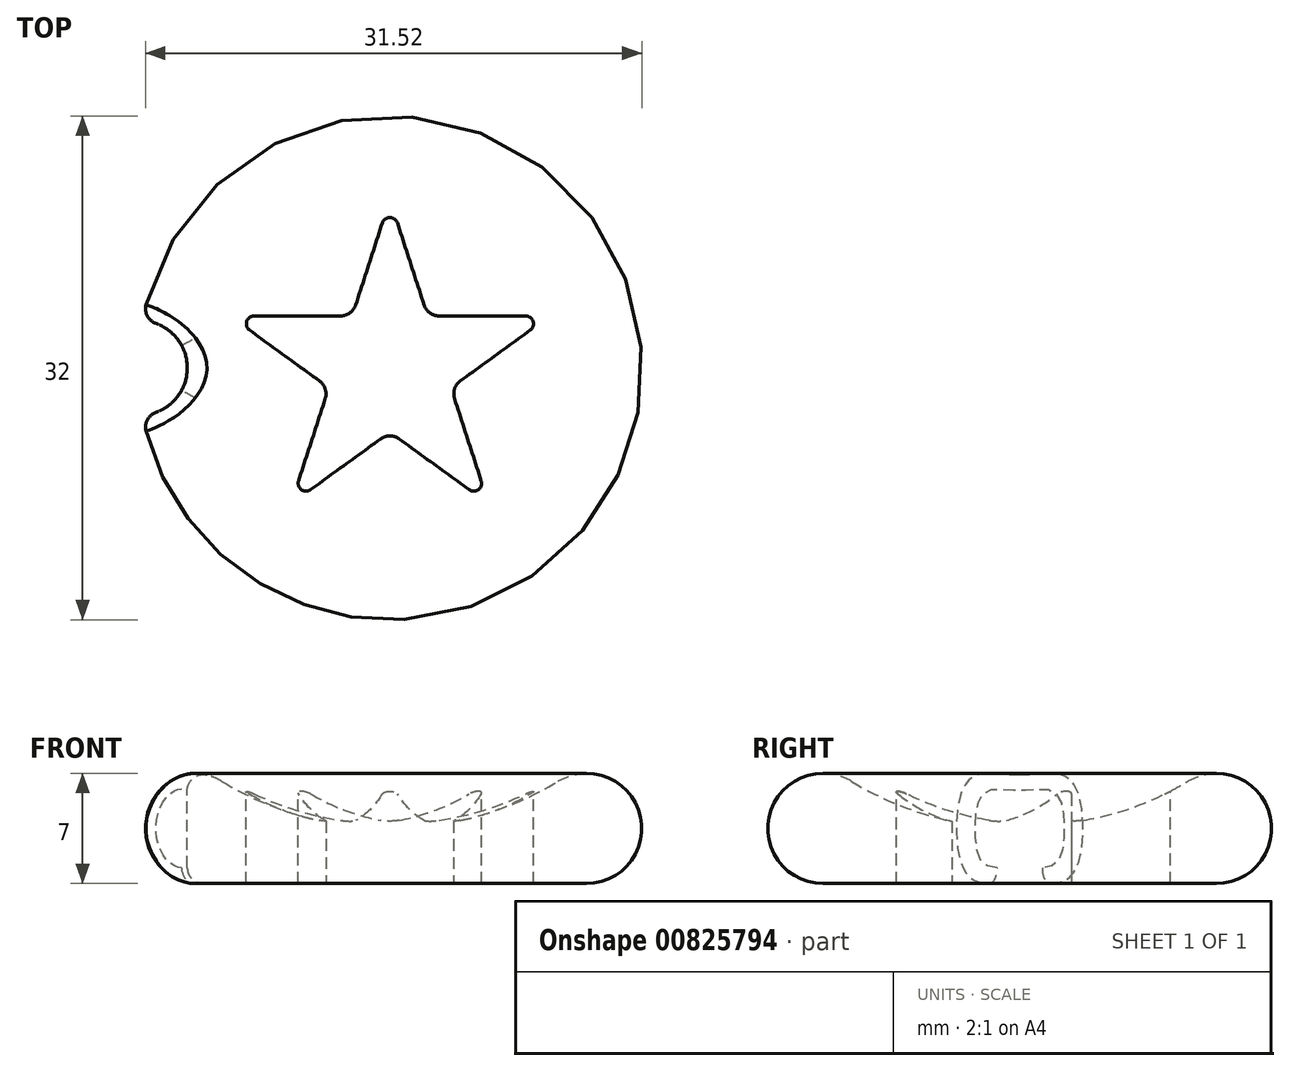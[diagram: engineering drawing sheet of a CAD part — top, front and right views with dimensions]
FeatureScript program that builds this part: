
annotation { "Feature Type Name" : "Feature", "Feature Type Description" : "" }
export const myFeature = defineFeature(function(context is Context, id is Id, definition is map)
    precondition{}
    {
        {
            var Q0;
            Q0=qCreatedBy(makeId("Front.planeOp"),FACE);
            var sketch = newSketch(context, id + "F0", { "sketchPlane" : qUnion([Q0])});
            skArc(sketch, "E0", {"start": v(-10.68, 6.5) * mm, "mid": v(-5.55, 4.26) * mm, "end": v(0, 3.5) * mm});
            skArc(sketch, "E1", {"start": v(-10.68, 6.5) * mm, "mid": v(-15.87, 4.44) * mm, "end": v(-12.5, 0) * mm});
            skLineSegment(sketch, "E2", {"start": v(0, 0) * mm, "end": v(-12.5, 0) * mm});
            skLineSegment(sketch, "E3", {"start": v(0, 0) * mm, "end": v(0, 3.5) * mm});
            skSolve(sketch);
        }
        {
            var Q0;
            Q0 = qSketchRegion(id + "F0", true);
            var Q1;
            Q1=sQuery(id+"F0.wireOp",EDGE,"E3");
            revolve(context, id + "F1", {"surfaceOperationType" : NewSurfaceOperationType.NEW, "entities" : qUnion([Q0]), "axis" : qUnion([Q1]), "revolveType" : RevolveType.FULL});
        }
        {
            var Q0;
            Q0=qCreatedBy(makeId("Top.planeOp"),FACE);
            var sketch = newSketch(context, id + "F2", { "sketchPlane" : qUnion([Q0])});
            skPoint(sketch, "E4.0", {"position": v(-15.87, 0) * mm});
            skCircle(sketch, "E5", {"center": v(-15.87, 0) * mm, "radius": 3 * mm});
            skSolve(sketch);
        }
        {
            var Q0;
            Q0=makeQuery(id+"F2.imprint","IMPRINT",FACE,{"disambiguationData":[TD([[makeQuery(id+"F2.imprint","IMPRINT",EDGE,{"derivedFrom":sQuery(id+"F2.wireOp",EDGE,"E5")}),1.0]])]});
            extrude(context, id + "F3", {"entities" : qUnion([Q0]), "operationType" : NewBodyOperationType.REMOVE, "endBound" : BoundingType.SYMMETRIC, "oppositeDirection" : true, "depth" : 50 * mm, "offsetDistance" : 25 * mm});
        }
        {
            var Q0;
            Q0=makeQuery(id+"F3.boolean.opBoolean","INTERSECT",EDGE,{"derivedFrom":[makeQuery(id+"F1.opRevolve","SWEPT_FACE",FACE,{"disambiguationData":[OSD([sQuery(id+"F0.wireOp",EDGE,"E1")])]}),makeQuery(id+"F3.opExtrude","SWEPT_FACE",FACE,{"disambiguationData":[OSD([sQuery(id+"F2.wireOp",EDGE,"E5")])]})]});
            fillet(context, id + "F4", {"entities" : qUnion([Q0]), "radius" : 1 * mm, "tangentPropagation" : true, "allowEdgeOverflow" : false});
        }
        {
            var Q0;
            Q0=qCreatedBy(makeId("Top.planeOp"),FACE);
            var sketch = newSketch(context, id + "F5", { "sketchPlane" : qUnion([Q0])});
            skCircle(sketch, "E6.0", {"center": v(0, 0) * mm, "radius": 10.68 * mm});
            skCircle(sketch, "E7.cCircle", {"center": v(0, 0) * mm, "radius": 10.68 * mm, "construction": true});
            skLineSegment(sketch, "E7.0", {"start": v(0, 10.68) * mm, "end": v(10.16, 3.3) * mm});
            skLineSegment(sketch, "E7.1", {"start": v(10.16, 3.3) * mm, "end": v(6.28, -8.64) * mm});
            skLineSegment(sketch, "E7.2", {"start": v(6.28, -8.64) * mm, "end": v(-6.28, -8.64) * mm});
            skLineSegment(sketch, "E7.3", {"start": v(-6.28, -8.64) * mm, "end": v(-10.16, 3.3) * mm});
            skLineSegment(sketch, "E7.4", {"start": v(-10.16, 3.3) * mm, "end": v(0, 10.68) * mm});
            skLineSegment(sketch, "E8", {"start": v(0, 10.68) * mm, "end": v(2.4, 3.3) * mm});
            skLineSegment(sketch, "E9", {"start": v(10.16, 3.3) * mm, "end": v(3.88, -1.26) * mm});
            skLineSegment(sketch, "E10", {"start": v(6.28, -8.64) * mm, "end": v(0, -4.08) * mm});
            skLineSegment(sketch, "E11", {"start": v(-6.28, -8.64) * mm, "end": v(-3.88, -1.26) * mm});
            skLineSegment(sketch, "E12", {"start": v(-10.16, 3.3) * mm, "end": v(-2.4, 3.3) * mm});
            skLineSegment(sketch, "E13.trimOffspring", {"start": v(2.4, 3.3) * mm, "end": v(10.16, 3.3) * mm});
            skLineSegment(sketch, "E14.trimOffspring", {"start": v(3.88, -1.26) * mm, "end": v(6.28, -8.64) * mm});
            skLineSegment(sketch, "E15.trimOffspring", {"start": v(0, -4.08) * mm, "end": v(-6.28, -8.64) * mm});
            skLineSegment(sketch, "E16.trimOffspring", {"start": v(-3.88, -1.26) * mm, "end": v(-10.16, 3.3) * mm});
            skLineSegment(sketch, "E17.trimOffspring", {"start": v(-2.4, 3.3) * mm, "end": v(0, 10.68) * mm});
            skSolve(sketch);
        }
        {
            var Q0;
            Q0=makeQuery(id+"F5.imprint","IMPRINT",FACE,{"disambiguationData":[TD([[makeQuery(id+"F5.imprint","IMPRINT",EDGE,{"derivedFrom":sQuery(id+"F5.wireOp",EDGE,"E8")}),-1.0]])]});
            extrude(context, id + "F6", {"entities" : qUnion([Q0]), "operationType" : NewBodyOperationType.REMOVE, "endBound" : BoundingType.THROUGH_ALL, "depth" : 25 * mm, "offsetDistance" : 25 * mm});
        }
        {
            var Q0;
            Q0=makeQuery(id+"F6.boolean.opBoolean","COPY",EDGE,{"derivedFrom":makeQuery(id+"F6.opExtrude","SWEPT_EDGE",EDGE,{"disambiguationData":[OSD([sQuery(id+"F5.wireOp",EDGE,"E12"),sQuery(id+"F5.wireOp",EDGE,"E17.trimOffspring")])]})});
            var Q1;
            Q1=makeQuery(id+"F6.boolean.opBoolean","COPY",EDGE,{"derivedFrom":makeQuery(id+"F6.opExtrude","SWEPT_EDGE",EDGE,{"disambiguationData":[OSD([sQuery(id+"F5.wireOp",EDGE,"E11"),sQuery(id+"F5.wireOp",EDGE,"E16.trimOffspring")])]})});
            var Q2;
            Q2=makeQuery(id+"F6.boolean.opBoolean","COPY",EDGE,{"derivedFrom":makeQuery(id+"F6.opExtrude","SWEPT_EDGE",EDGE,{"disambiguationData":[OSD([sQuery(id+"F5.wireOp",EDGE,"E10"),sQuery(id+"F5.wireOp",EDGE,"E15.trimOffspring")])]})});
            var Q3;
            Q3=makeQuery(id+"F6.boolean.opBoolean","COPY",EDGE,{"derivedFrom":makeQuery(id+"F6.opExtrude","SWEPT_EDGE",EDGE,{"disambiguationData":[OSD([sQuery(id+"F5.wireOp",EDGE,"E9"),sQuery(id+"F5.wireOp",EDGE,"E14.trimOffspring")])]})});
            var Q4;
            Q4=makeQuery(id+"F6.boolean.opBoolean","COPY",EDGE,{"derivedFrom":makeQuery(id+"F6.opExtrude","SWEPT_EDGE",EDGE,{"disambiguationData":[OSD([sQuery(id+"F5.wireOp",EDGE,"E8"),sQuery(id+"F5.wireOp",EDGE,"E13.trimOffspring")])]})});
            fillet(context, id + "F7", {"entities" : qUnion([Q0, Q1, Q2, Q3, Q4]), "radius" : 1 * mm, "tangentPropagation" : true, "allowEdgeOverflow" : false});
        }
        {
            var Q0;
            Q0=makeQuery(id+"F6.boolean.opBoolean","COPY",EDGE,{"derivedFrom":makeQuery(id+"F6.opExtrude","SWEPT_EDGE",EDGE,{"disambiguationData":[OSD([sQuery(id+"F5.wireOp",EDGE,"E6.0"),sQuery(id+"F5.wireOp",EDGE,"E7.2"),sQuery(id+"F5.wireOp",EDGE,"E7.3"),sQuery(id+"F5.wireOp",EDGE,"E11"),sQuery(id+"F5.wireOp",EDGE,"E15.trimOffspring")])]})});
            var Q1;
            Q1=makeQuery(id+"F6.boolean.opBoolean","COPY",EDGE,{"derivedFrom":makeQuery(id+"F6.opExtrude","SWEPT_EDGE",EDGE,{"disambiguationData":[OSD([sQuery(id+"F5.wireOp",EDGE,"E6.0"),sQuery(id+"F5.wireOp",EDGE,"E7.3"),sQuery(id+"F5.wireOp",EDGE,"E7.4"),sQuery(id+"F5.wireOp",EDGE,"E12"),sQuery(id+"F5.wireOp",EDGE,"E16.trimOffspring")])]})});
            var Q2;
            Q2=makeQuery(id+"F6.boolean.opBoolean","COPY",EDGE,{"derivedFrom":makeQuery(id+"F6.opExtrude","SWEPT_EDGE",EDGE,{"disambiguationData":[OSD([sQuery(id+"F5.wireOp",EDGE,"E6.0"),sQuery(id+"F5.wireOp",EDGE,"E7.0"),sQuery(id+"F5.wireOp",EDGE,"E7.1"),sQuery(id+"F5.wireOp",EDGE,"E9"),sQuery(id+"F5.wireOp",EDGE,"E13.trimOffspring")])]})});
            var Q3;
            Q3=makeQuery(id+"F6.boolean.opBoolean","COPY",EDGE,{"derivedFrom":makeQuery(id+"F6.opExtrude","SWEPT_EDGE",EDGE,{"disambiguationData":[OSD([sQuery(id+"F5.wireOp",EDGE,"E6.0"),sQuery(id+"F5.wireOp",EDGE,"E7.1"),sQuery(id+"F5.wireOp",EDGE,"E7.2"),sQuery(id+"F5.wireOp",EDGE,"E10"),sQuery(id+"F5.wireOp",EDGE,"E14.trimOffspring")])]})});
            var Q4;
            Q4=makeQuery(id+"F6.boolean.opBoolean","COPY",EDGE,{"derivedFrom":makeQuery(id+"F6.opExtrude","SWEPT_EDGE",EDGE,{"disambiguationData":[OSD([sQuery(id+"F5.wireOp",EDGE,"E6.0"),sQuery(id+"F5.wireOp",EDGE,"E7.0"),sQuery(id+"F5.wireOp",EDGE,"E7.4"),sQuery(id+"F5.wireOp",EDGE,"E8"),sQuery(id+"F5.wireOp",EDGE,"E17.trimOffspring")])]})});
            fillet(context, id + "F8", {"entities" : qUnion([Q0, Q1, Q2, Q3, Q4]), "radius" : 0.5 * mm, "tangentPropagation" : true, "allowEdgeOverflow" : false});
        }
    });
